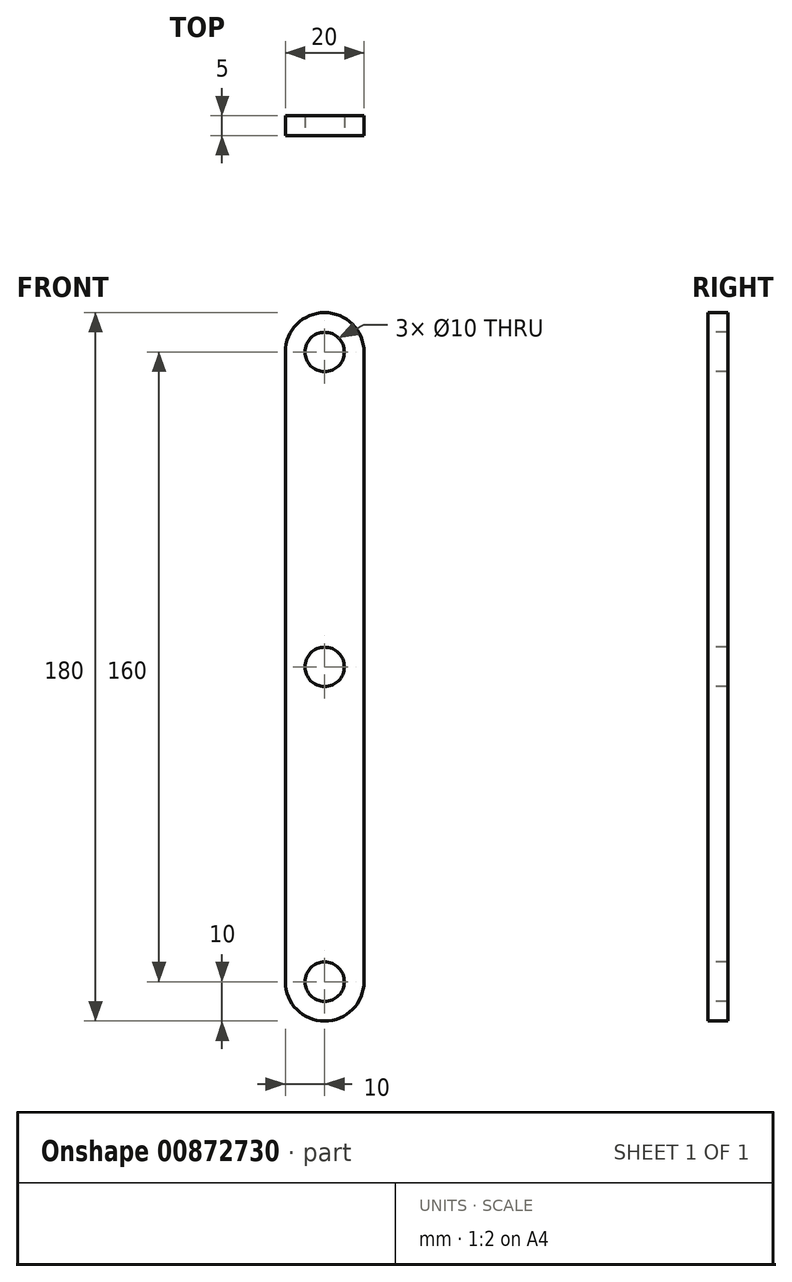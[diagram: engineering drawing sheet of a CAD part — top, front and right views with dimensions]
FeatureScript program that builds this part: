
annotation { "Feature Type Name" : "Feature", "Feature Type Description" : "" }
export const myFeature = defineFeature(function(context is Context, id is Id, definition is map)
    precondition{}
    {
        {
            var Q0;
            Q0=qCreatedBy(makeId("Front.planeOp"),FACE);
            var sketch = newSketch(context, id + "F0", { "sketchPlane" : qUnion([Q0])});
            skCircle(sketch, "E0", {"center": v(0, 80) * mm, "radius": 10 * mm});
            skCircle(sketch, "E1", {"center": v(0, -80) * mm, "radius": 10 * mm});
            skLineSegment(sketch, "E2", {"start": v(10, 80) * mm, "end": v(10, -80) * mm});
            skLineSegment(sketch, "E3", {"start": v(-10, 80) * mm, "end": v(-10, -80) * mm});
            skSolve(sketch);
        }
        {
            var Q0;
            Q0 = qSketchRegion(id + "F0", true);
            extrude(context, id + "F1", {"entities" : qUnion([Q0]), "depth" : 5 * mm, "offsetDistance" : 25 * mm});
        }
        {
            var Q0;
            Q0=makeQuery(id+"F1.opExtrude","CAP_FACE",FACE,{"disambiguationData":[OSD([sQuery(id+"F0.wireOp",EDGE,"E0"),sQuery(id+"F0.wireOp",EDGE,"E1"),sQuery(id+"F0.wireOp",EDGE,"E2"),sQuery(id+"F0.wireOp",EDGE,"E3")])],"isStart":false});
            var sketch = newSketch(context, id + "F2", { "sketchPlane" : qUnion([Q0])});
            skCircle(sketch, "E4", {"center": v(0, 80) * mm, "radius": 5 * mm});
            skCircle(sketch, "E5", {"center": v(0, -80) * mm, "radius": 5 * mm});
            skCircle(sketch, "E6", {"center": v(0, 0) * mm, "radius": 5 * mm});
            skSolve(sketch);
        }
        {
            var Q0;
            Q0 = qSketchRegion(id + "F2", true);
            extrude(context, id + "F3", {"entities" : qUnion([Q0]), "operationType" : NewBodyOperationType.REMOVE, "oppositeDirection" : true, "depth" : 25 * mm, "offsetDistance" : 25 * mm});
        }
    });
